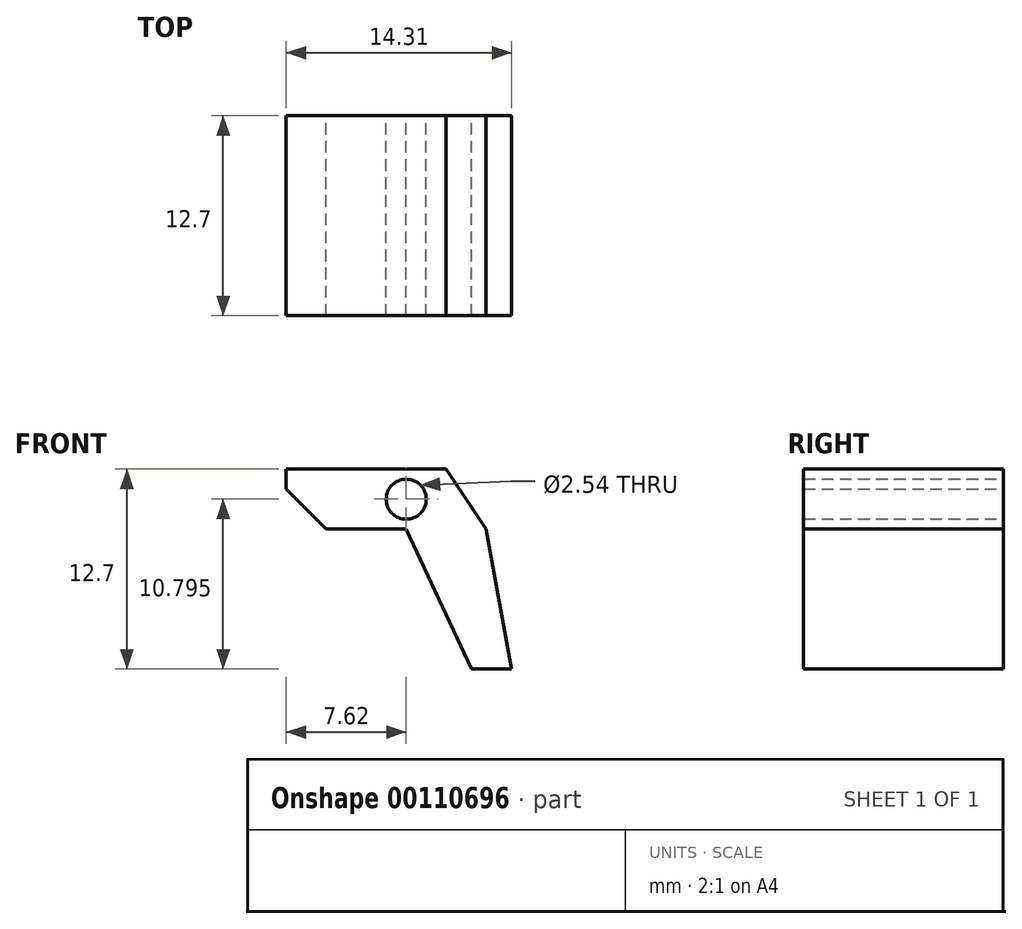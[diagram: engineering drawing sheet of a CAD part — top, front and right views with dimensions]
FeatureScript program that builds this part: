
annotation { "Feature Type Name" : "Feature", "Feature Type Description" : "" }
export const myFeature = defineFeature(function(context is Context, id is Id, definition is map)
    precondition{}
    {
        {
            var Q0;
            Q0=qCreatedBy(makeId("Front.planeOp"),FACE);
            var sketch = newSketch(context, id + "F0", { "sketchPlane" : qUnion([Q0])});
            skLineSegment(sketch, "E0", {"start": v(0, 0) * mm, "end": v(-10.16, 0) * mm});
            skLineSegment(sketch, "E1", {"start": v(-10.16, 0) * mm, "end": v(-10.16, -1.27) * mm});
            skLineSegment(sketch, "E2", {"start": v(-10.16, -1.27) * mm, "end": v(-7.62, -3.81) * mm});
            skLineSegment(sketch, "E3", {"start": v(-7.62, -3.81) * mm, "end": v(-2.54, -3.81) * mm});
            skCircle(sketch, "E4", {"center": v(-2.54, -1.9) * mm, "radius": 1.27 * mm});
            skLineSegment(sketch, "E5", {"start": v(4.15, -12.7) * mm, "end": v(1.6, -12.7) * mm});
            skLineSegment(sketch, "E6", {"start": v(1.6, -12.7) * mm, "end": v(-2.54, -3.8) * mm});
            skLineSegment(sketch, "E7", {"start": v(2.54, -3.8) * mm, "end": v(4.15, -12.7) * mm});
            skLineSegment(sketch, "E8.bottom", {"start": v(-7.62, 0) * mm, "end": v(-5.08, 0) * mm});
            skLineSegment(sketch, "E8.right", {"start": v(-5.08, 0) * mm, "end": v(-5.08, 3.17) * mm});
            skLineSegment(sketch, "E9", {"start": v(-7.62, 0) * mm, "end": v(-5.08, 3.18) * mm});
            skLineSegment(sketch, "E10", {"start": v(0, 0) * mm, "end": v(2.54, -3.8) * mm});
            skSolve(sketch);
        }
        {
            var Q0;
            Q0=makeQuery(id+"F0.imprint","IMPRINT",FACE,{"disambiguationData":[TD([[makeQuery(id+"F0.imprint","IMPRINT",EDGE,{"derivedFrom":sQuery(id+"F0.wireOp",EDGE,"E0")}),1.0]])]});
            var Q1;
            Q1=makeQuery(id+"F0.imprint","IMPRINT",FACE,{"disambiguationData":[TD([[makeQuery(id+"F0.imprint","IMPRINT",EDGE,{"derivedFrom":sQuery(id+"F0.wireOp",EDGE,"oS7793MD-U2AM-7vlL-HP6H-aRzdyVr9nu6F.bottom")}),-1.0]])]});
            var Q2;
            Q2=makeQuery(id+"F0.imprint","IMPRINT",FACE,{"disambiguationData":[TD([[makeQuery(id+"F0.imprint","IMPRINT",EDGE,{"derivedFrom":sQuery(id+"F0.wireOp",EDGE,"E8.bottom")}),1.0]])]});
            extrude(context, id + "F1", {"entities" : qUnion([Q0, Q1, Q2]), "depth" : 12.7 * mm});
        }
    });
